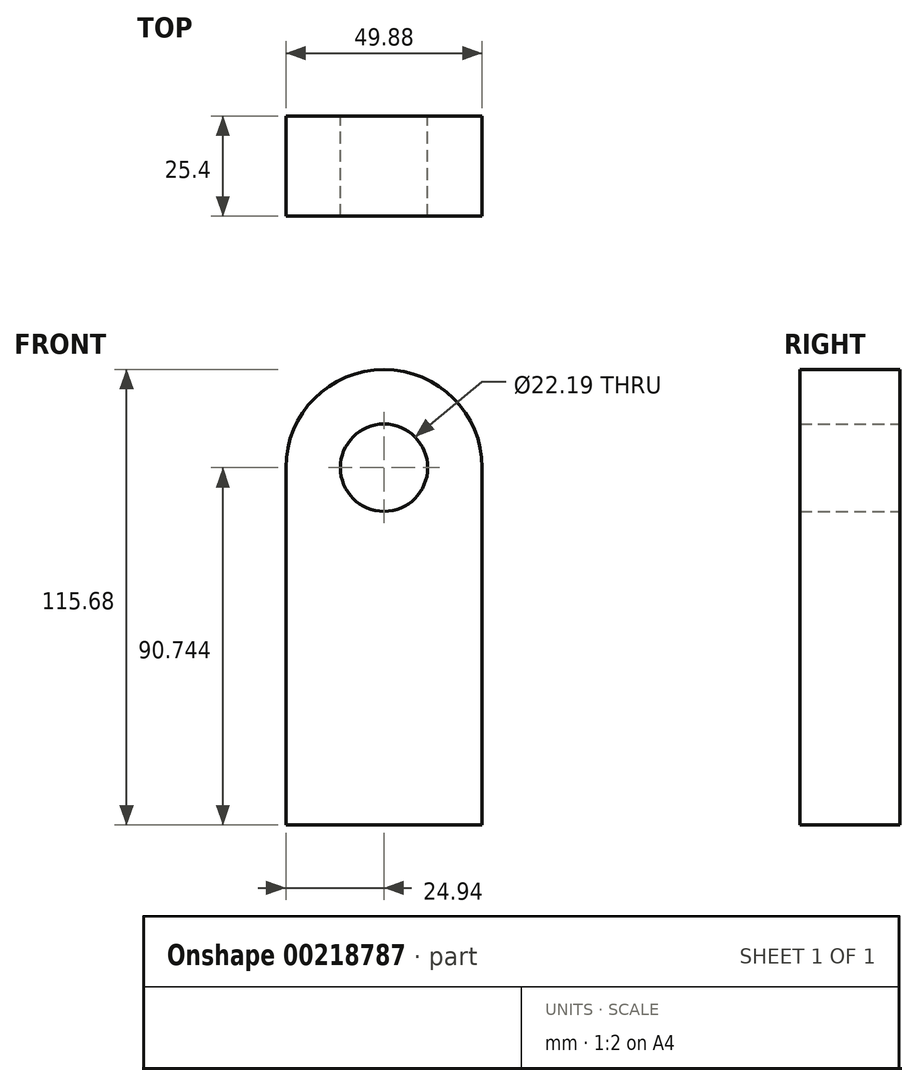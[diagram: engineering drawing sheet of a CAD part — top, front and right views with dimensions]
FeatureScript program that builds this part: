
annotation { "Feature Type Name" : "Feature", "Feature Type Description" : "" }
export const myFeature = defineFeature(function(context is Context, id is Id, definition is map)
    precondition{}
    {
        {
            var Q0;
            Q0=qCreatedBy(makeId("Front.planeOp"),FACE);
            var sketch = newSketch(context, id + "F0", { "sketchPlane" : qUnion([Q0])});
            skLineSegment(sketch, "E0.top", {"start": v(-24.94, -45.37) * mm, "end": v(24.94, -45.37) * mm});
            skLineSegment(sketch, "E0.left", {"start": v(-24.94, 45.37) * mm, "end": v(-24.94, -45.37) * mm});
            skLineSegment(sketch, "E0.right", {"start": v(24.94, 45.37) * mm, "end": v(24.94, -45.37) * mm});
            skPoint(sketch, "E0.middle", {"position": v(0, 0) * mm});
            skArc(sketch, "E1", {"start": v(24.94, 45.37) * mm, "mid": v(0, 70.31) * mm, "end": v(-24.94, 45.37) * mm});
            skCircle(sketch, "E2", {"center": v(0, 45.37) * mm, "radius": 11.1 * mm});
            skSolve(sketch);
        }
        {
            var Q0;
            Q0=makeQuery(id+"F0.imprint","IMPRINT",FACE,{"disambiguationData":[TD([[makeQuery(id+"F0.imprint","IMPRINT",EDGE,{"derivedFrom":sQuery(id+"F0.wireOp",EDGE,"E0.top")}),1.0]])]});
            extrude(context, id + "F1", {"entities" : qUnion([Q0]), "depth" : 25.4 * mm});
        }
    });
